# Revit family: RS776KDuschrinne
name_source: partatom
category: Sanitärinstallationen
units: mm (PartAtom-declared; Revit-internal decimal feet)

## family parameters
Arbeitsebenenbasiert = Nein
Beim Laden mit Abzugskörper schneiden = Nein
Bemaßung runder Anschluss = Durchmesser verwenden
Gemeinsam genutzt = Nein
Immer vertikal = Ja
Raumberechnungspunkt = Nein
Teiletyp = Normal

## types (2) — shared parameters
Baugruppenkennzeichen = D2030300
Hersteller = Resitec
RS_DN1 = 100 mm  [stored 0.328084 ft]
RS_Manufacture = Resitec
RS_URL = https://resitec.ch
RS_dia001 = 228 mm
RS_dia002 = 110 mm  [stored 0.360892 ft]
RS_dimk001 = 115 mm  [stored 0.377297 ft]
RS_s001 = 3 mm  [stored 0.00984252 ft]
RS_s002 = 2 mm  [stored 0.00656168 ft]
URL = https://www.resitec.ch
zero-valued in all types: Anschlusswert DU L/s, RS_DN2, Vorgabe-Ansicht

## type names (no varying parameters)
- Rand 18mm
- Rand 4.5

note: [stored X ft] marks values corroborated as IEEE doubles in the binary element streams (Revit-internal decimal feet)

## geometry (parser evidence)
native form markers: Blend x4
no freeform markers — native parametric forms only
